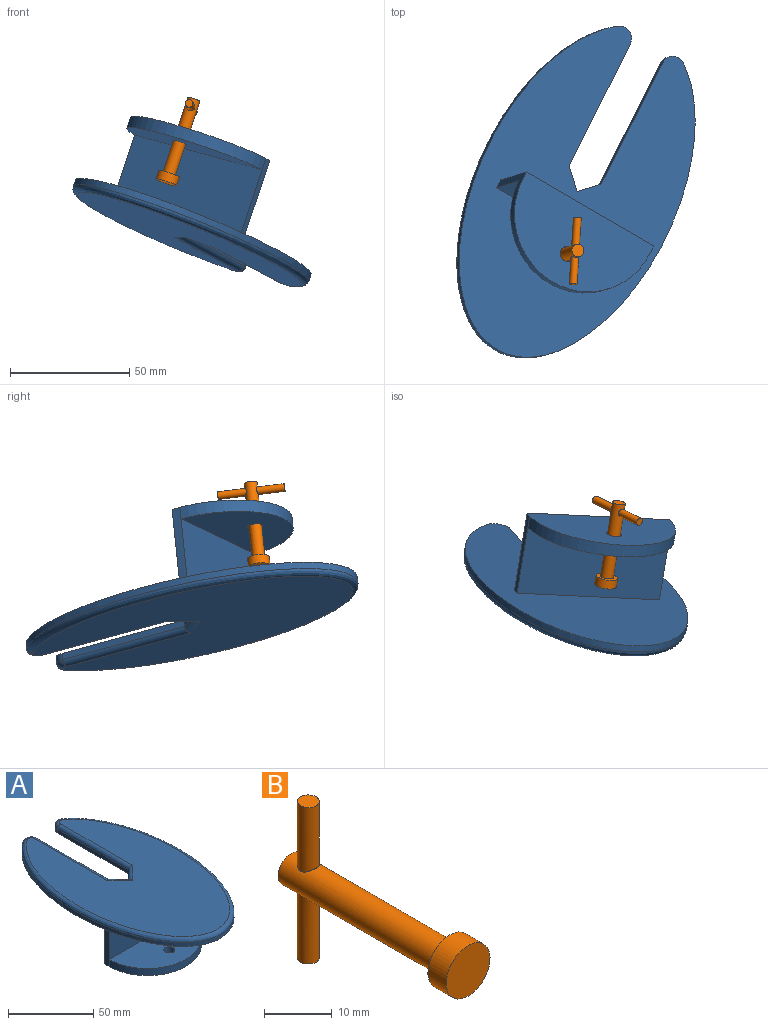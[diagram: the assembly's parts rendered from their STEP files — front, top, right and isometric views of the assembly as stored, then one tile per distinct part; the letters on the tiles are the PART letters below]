
ASSEMBLY  parts=2 mates=1
PART A: 24 faces, bbox 86.4x148.9x39.7 mm
  f0: plane 63.42x29.33mm, normal (0,-1,0), area 1860.3mm2, adj f7,f17,f18,f22
  f1: plane 143.38x81.31mm, normal (0,0,1), area 7892.7mm2, adj f8,f9,f10,f11,f12,f14,f16
  f2: plane 58.85x2.76mm, normal (1,0,0), area 162.2mm2, adj f6,f7,f8,f15
  f3: extruded ~147.53x86.36mm, area 960.8mm2, adj f7,f9,f13,f15
  f4: plane 58.55x2.76mm, normal (-1,0,0), area 161.4mm2, adj f5,f7,f11,f13
  f5: plane 8.29x8.08mm, normal (-0.7,0.72,0), area 31.9mm2, adj f4,f6,f7,f12
  f6: plane 8.08x7.87mm, normal (0.72,0.7,0), area 31.1mm2, adj f2,f5,f7,f10
  f7: plane 148.45x86.38mm, normal (0,0,-1), area 8936.2mm2, adj f0,f2,f3,f4,f5,f6,f13,f15
  f8: cylinder r=2.54mm len=59.89mm, axis (0,-1,0), area 236.3mm2, adj f1,f2,f10,f16
  f9: bspline ~148.5x86.39mm, area 1372.5mm2, adj f1,f3,f14,f16
  f10: cylinder r=2.54mm len=12.41mm, axis (0.7,-0.72,0), area 50.2mm2, adj f1,f6,f8,f12
  f11: cylinder r=2.54mm len=59.63mm, axis (0,1,0), area 235.2mm2, adj f1,f4,f12,f14
  f12: cylinder r=2.54mm len=12.65mm, axis (0.72,0.7,0), area 51.4mm2, adj f1,f5,f10,f11
  f13: cylinder r=5.08mm len=8.06mm, axis (0,0,-1), area 30.8mm2, adj f3,f4,f7,f14
  f14: torus R=2.54mm, axis (0,0,1), area 36.4mm2, adj f1,f9,f11,f13
  f15: cylinder r=5.08mm len=7.99mm, axis (0,0,-1), area 30.5mm2, adj f2,f3,f7,f16
  f16: torus R=2.54mm, axis (0,0,1), area 36.2mm2, adj f1,f8,f9,f15
  f17: plane 34.41x3.73mm, normal (1,0,0), area 128.4mm2, adj f0,f7,f19,f20,f21
  f18: plane 34.41x3.73mm, normal (-1,0,0), area 128.4mm2, adj f0,f7,f19,f20,f21
  f19: plane 63.42x34.41mm, normal (0,1,0), area 2182.5mm2, adj f7,f17,f18,f20
  f20: plane 63.42x35.44mm, normal (0,0,-1), area 1784.4mm2, adj f17,f18,f19,f21,f23
  f21: cylinder r=31.71mm len=63.42mm, axis (0,0,-1), area 506.1mm2, adj f17,f18,f20,f22
  f22: plane 63.42x31.71mm, normal (0,0,1), area 1547.8mm2, adj f0,f21,f23
  f23: cylinder r=3.17mm len=6.35mm, axis (0,0,-1), area 101.3mm2, adj f20,f22
PART B: 9 faces, bbox 9.1x36.9x28.2 mm
  f0: cylinder r=2.68mm len=33.06mm, axis (0,1,0), area 538.7mm2, adj f1,f4,f6,f7
  f1: plane 5.35x5.35mm, normal (0,1,0), area 22.5mm2, adj f0
  f2: cylinder r=4.55mm len=9.11mm, axis (0,1,0), area 109mm2, adj f3,f4
  f3: plane 9.11x9.11mm, normal (0,-1,0), area 65.1mm2, adj f2
  f4: plane 9.11x9.11mm, normal (0,1,0), area 42.6mm2, adj f0,f2
  f5: plane 3.23x3.23mm, normal (0,0,-1), area 8.2mm2, adj f6
  f6: cylinder r=1.61mm len=12.1mm, axis (0,0,-1), area 119.9mm2, adj f0,f5
  f7: cylinder r=1.61mm len=11.79mm, axis (0,0,-1), area 116.7mm2, adj f0,f8
  f8: plane 3.23x3.23mm, normal (0,0,1), area 8.2mm2, adj f7
PLACE A rot(axis=(-0.25,-0.97,0.09),163.6deg) t=(-179.87,147.33,-148.36)mm
PLACE B rot(axis=(0.97,0.12,-0.21),85.2deg) t=(-179.56,122.47,-94.64)mm
MATE revolute A.f23 <-> B.f0  axis (0.32,0.1,0.94) through (-184.77,120.87,-110.25)mm
